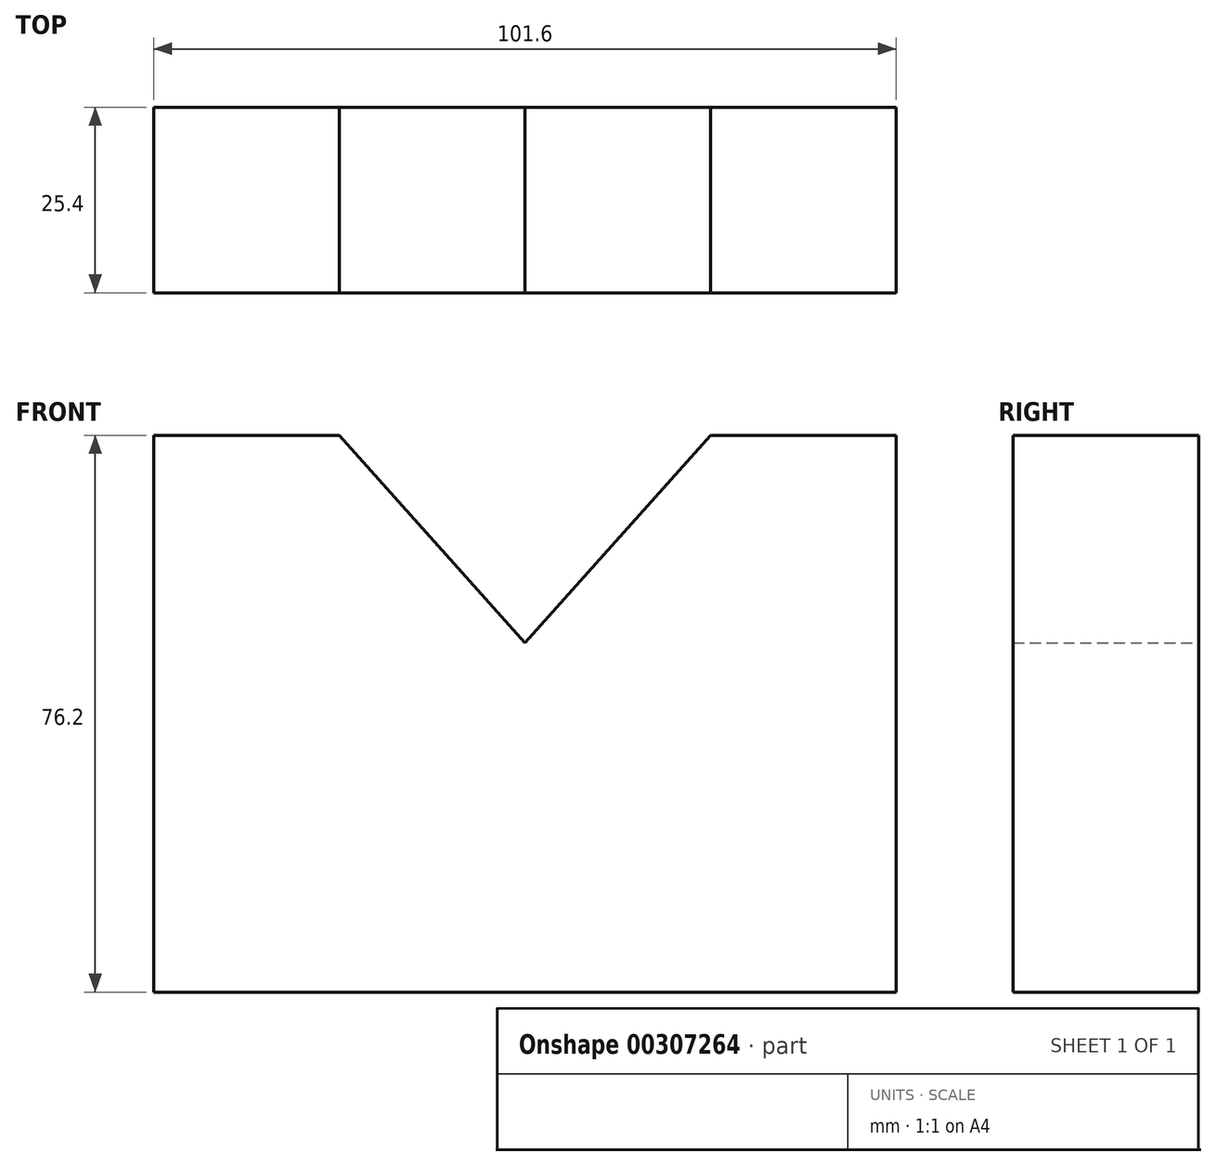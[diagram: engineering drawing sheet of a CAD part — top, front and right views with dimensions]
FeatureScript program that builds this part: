
annotation { "Feature Type Name" : "Feature", "Feature Type Description" : "" }
export const myFeature = defineFeature(function(context is Context, id is Id, definition is map)
    precondition{}
    {
        {
            var Q0;
            Q0=qCreatedBy(makeId("Front.planeOp"),FACE);
            var sketch = newSketch(context, id + "F0", { "sketchPlane" : qUnion([Q0])});
            skLineSegment(sketch, "E0", {"start": v(-50.8, -31.63) * mm, "end": v(50.8, -31.63) * mm});
            skLineSegment(sketch, "E1", {"start": v(50.8, -31.63) * mm, "end": v(50.8, 44.57) * mm});
            skLineSegment(sketch, "E2", {"start": v(25.4, 44.57) * mm, "end": v(50.8, 44.57) * mm});
            skLineSegment(sketch, "E3", {"start": v(25.4, 44.57) * mm, "end": v(0, 16.17) * mm});
            skLineSegment(sketch, "E4", {"start": v(0, 16.17) * mm, "end": v(-25.4, 44.57) * mm});
            skLineSegment(sketch, "E5", {"start": v(-25.4, 44.57) * mm, "end": v(-50.8, 44.57) * mm});
            skLineSegment(sketch, "E6", {"start": v(-50.8, 44.57) * mm, "end": v(-50.8, -31.63) * mm});
            skSolve(sketch);
        }
        {
            var Q0;
            Q0=makeQuery(id+"F0.imprint","IMPRINT",FACE,{"disambiguationData":[TD([[makeQuery(id+"F0.imprint","IMPRINT",EDGE,{"derivedFrom":sQuery(id+"F0.wireOp",EDGE,"E0")}),1.0]])]});
            extrude(context, id + "F1", {"entities" : qUnion([Q0]), "depth" : 25.4 * mm});
        }
    });
